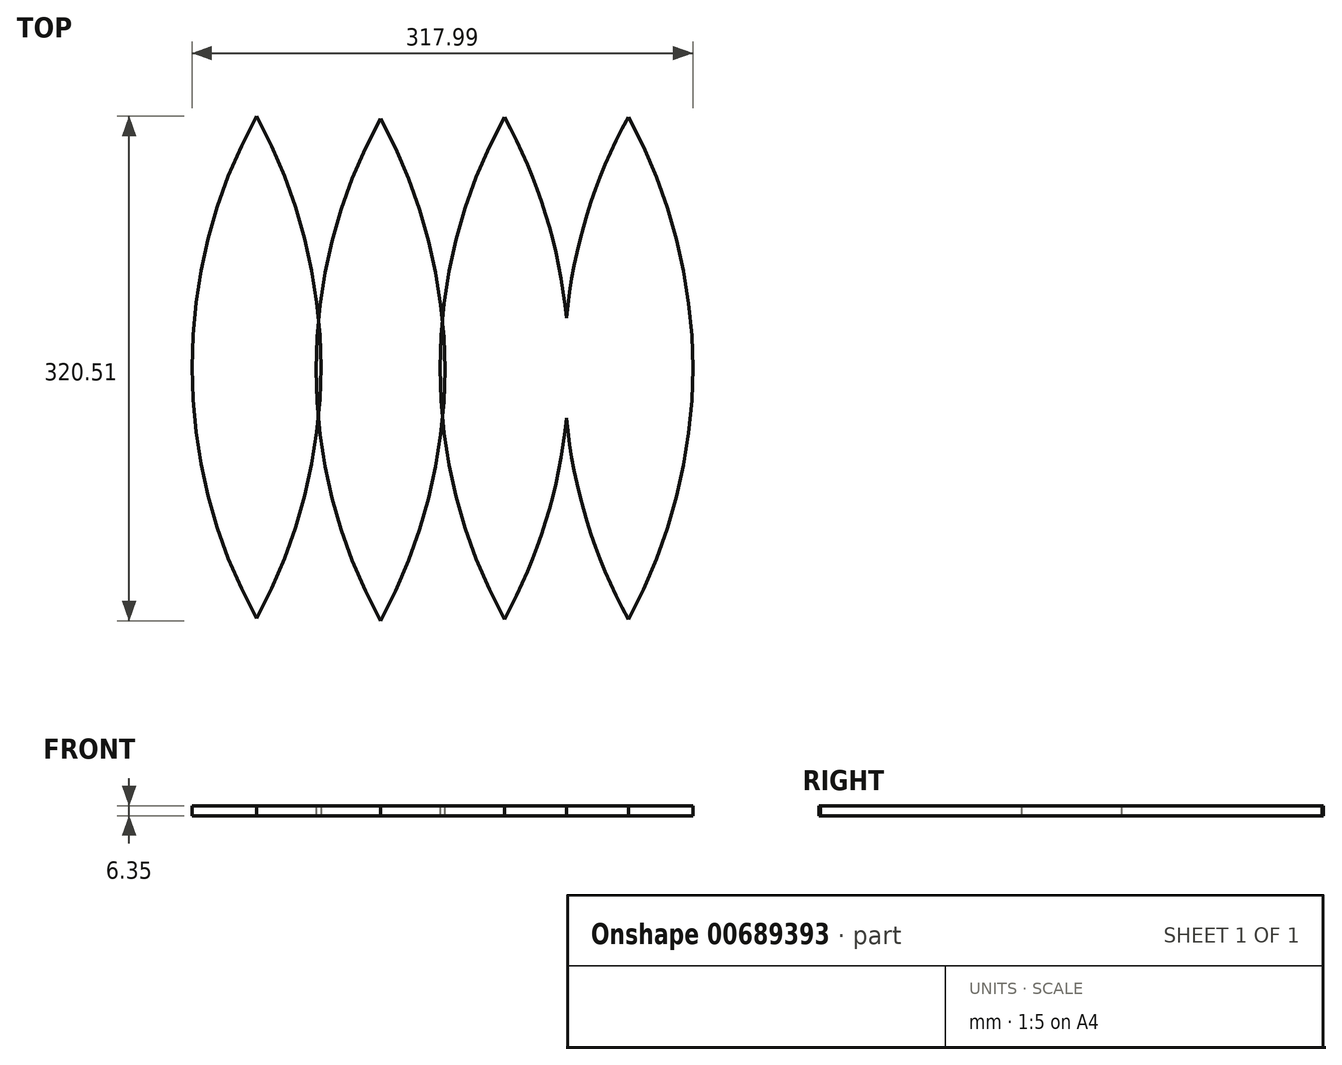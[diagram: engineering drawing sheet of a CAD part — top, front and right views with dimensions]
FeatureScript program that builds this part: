
annotation { "Feature Type Name" : "Feature", "Feature Type Description" : "" }
export const myFeature = defineFeature(function(context is Context, id is Id, definition is map)
    precondition{}
    {
        {
            var Q0;
            Q0=qCreatedBy(makeId("Top.planeOp"),FACE);
            var sketch = newSketch(context, id + "F0", { "sketchPlane" : qUnion([Q0])});
            skLineSegment(sketch, "E0", {"start": v(-118.27, 160.01) * mm, "end": v(-118.27, -159.01) * mm});
            skArc(sketch, "E1", {"start": v(-118.27, 160.01) * mm, "mid": v(-159.15, 0.5) * mm, "end": v(-118.27, -159.01) * mm});
            skArc(sketch, "E2", {"start": v(-118.27, -159.01) * mm, "mid": v(-77.38, 0.5) * mm, "end": v(-118.27, 160.01) * mm});
            skSolve(sketch);
        }
        {
            var Q0;
            Q0=qCreatedBy(makeId("Top.planeOp"),FACE);
            var sketch = newSketch(context, id + "F1", { "sketchPlane" : qUnion([Q0])});
            skLineSegment(sketch, "E3", {"start": v(-39.53, 158.53) * mm, "end": v(-39.53, -160.5) * mm});
            skArc(sketch, "E4", {"start": v(-39.53, 158.53) * mm, "mid": v(-80.41, -0.98) * mm, "end": v(-39.53, -160.5) * mm});
            skArc(sketch, "E5", {"start": v(-39.53, -160.5) * mm, "mid": v(1.36, -0.98) * mm, "end": v(-39.53, 158.53) * mm});
            skSolve(sketch);
        }
        {
            var Q0;
            Q0=qCreatedBy(makeId("Top.planeOp"),FACE);
            var sketch = newSketch(context, id + "F2", { "sketchPlane" : qUnion([Q0])});
            skLineSegment(sketch, "E6", {"start": v(39.21, 159.51) * mm, "end": v(39.21, -159.51) * mm});
            skArc(sketch, "E7", {"start": v(39.21, 159.51) * mm, "mid": v(-1.67, 0) * mm, "end": v(39.21, -159.51) * mm});
            skArc(sketch, "E8", {"start": v(39.21, -159.51) * mm, "mid": v(80.1, 0) * mm, "end": v(39.21, 159.51) * mm});
            skLineSegment(sketch, "E9", {"start": v(117.95, 159.51) * mm, "end": v(117.95, -159.51) * mm});
            skArc(sketch, "E10", {"start": v(117.95, 159.51) * mm, "mid": v(77.07, 0) * mm, "end": v(117.95, -159.51) * mm});
            skArc(sketch, "E11", {"start": v(117.95, -159.51) * mm, "mid": v(158.84, 0) * mm, "end": v(117.95, 159.51) * mm});
            skSolve(sketch);
        }
        {
            var Q0;
            Q0=qSketchRegion(id+"F1",true);
            var Q1;
            Q1=qSketchRegion(id+"F2",true);
            var Q2;
            Q2=qSketchRegion(id+"F0",true);
            extrude(context, id + "F3", {"entities" : qUnion([Q0, Q1, Q2]), "depth" : 6.35 * mm, "offsetDistance" : 25.4 * mm});
        }
    });
